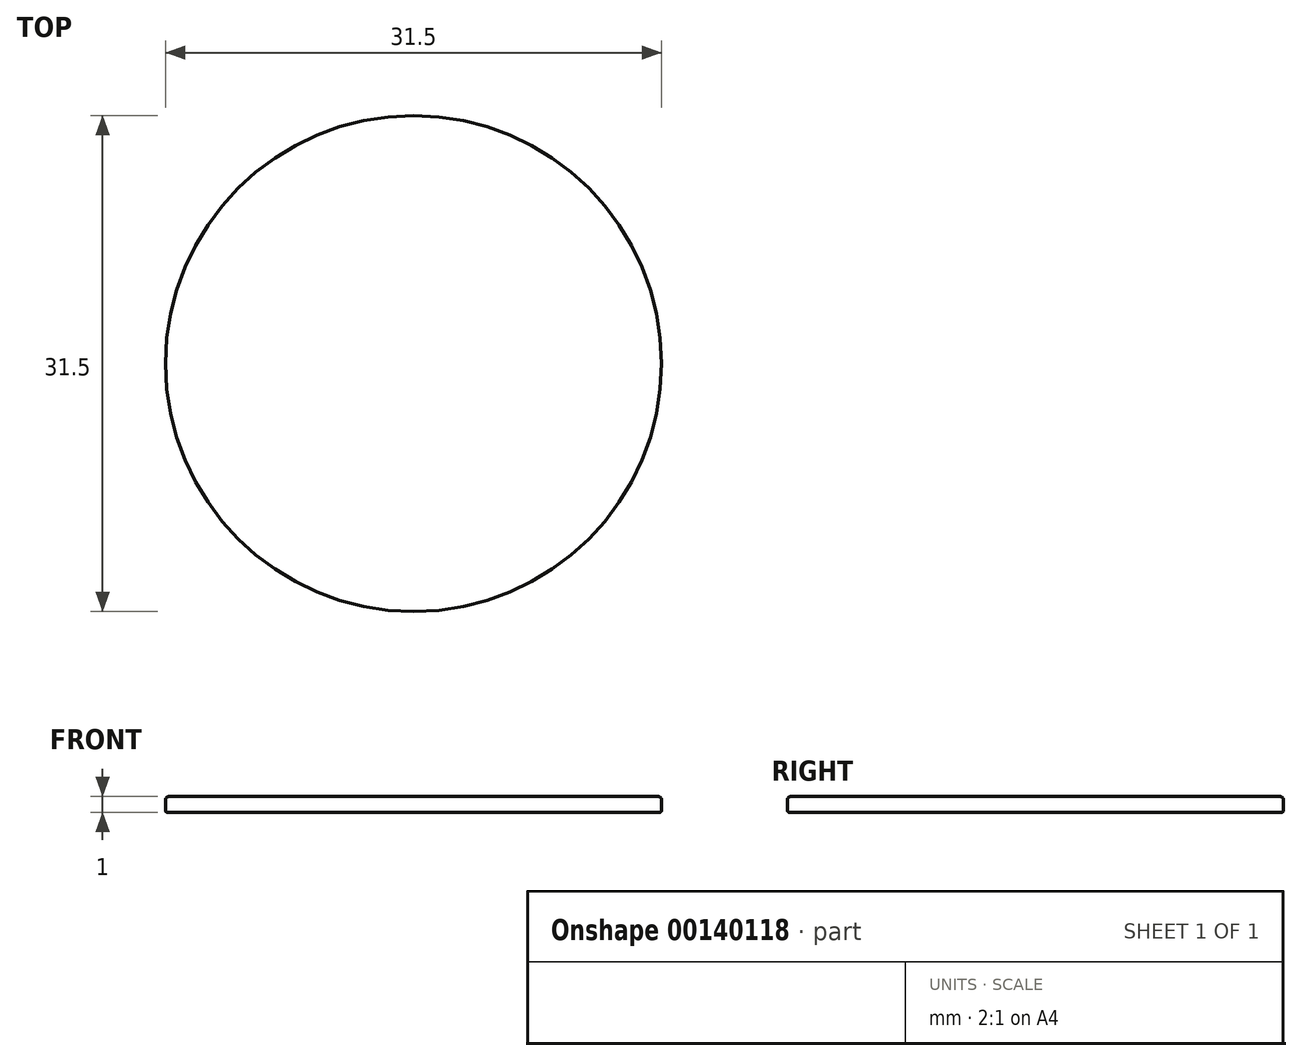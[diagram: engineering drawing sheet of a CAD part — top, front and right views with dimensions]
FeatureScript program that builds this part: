
annotation { "Feature Type Name" : "Feature", "Feature Type Description" : "" }
export const myFeature = defineFeature(function(context is Context, id is Id, definition is map)
    precondition{}
    {
        {
            var Q0;
            Q0=qCreatedBy(makeId("Top.planeOp"),FACE);
            var sketch = newSketch(context, id + "F0", { "sketchPlane" : qUnion([Q0])});
            skCircle(sketch, "E0", {"center": v(0, 0) * mm, "radius": 15.75 * mm});
            skSolve(sketch);
        }
        {
            var Q0;
            Q0 = qSketchRegion(id + "F0", true);
            extrude(context, id + "F1", {"entities" : qUnion([Q0]), "depth" : 1 * mm});
        }
        {
            var Q0;
            Q0=makeQuery(id+"F1.opExtrude","CAP_EDGE",EDGE,{"disambiguationData":[OSD([sQuery(id+"F0.wireOp",EDGE,"E0")])],"isStart":true});
            fillet(context, id + "F2", {"entities" : qUnion([Q0]), "radius" : .1 * mm, "tangentPropagation" : true, "allowEdgeOverflow" : false});
        }
        {
            var Q0;
            Q0=makeQuery(id+"F1.opExtrude","CAP_EDGE",EDGE,{"disambiguationData":[OSD([sQuery(id+"F0.wireOp",EDGE,"E0")])],"isStart":false});
            var Q1;
            Q1=makeQuery(id+"F1.opExtrude","CAP_EDGE",EDGE,{"disambiguationData":[OSD([sQuery(id+"F0.wireOp",EDGE,"E0")])],"isStart":false});
            fillet(context, id + "F3", {"entities" : qUnion([Q0, Q1]), "radius" : .2 * mm, "tangentPropagation" : true, "allowEdgeOverflow" : false});
        }
    });
